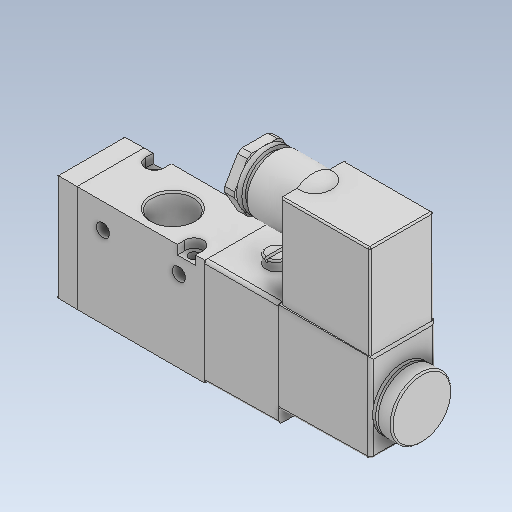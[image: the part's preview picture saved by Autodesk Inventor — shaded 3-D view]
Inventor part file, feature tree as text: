
AUTODESK INVENTOR PART (.ipt)
format: ipt  version: 2020 (Build 240168000, 168)  size: 314,368 bytes
history: native  units: in
note: dims shown in document units (in); Inventor stores cm internally (conversion verified against a paired STEP export)
features: fillet x3, chamfer x1
ambient origin geometry x8: Origin, YZ Plane, XZ Plane, XY Plane, X Axis, Y Axis, Z Axis, Center Point
bodies: Solid1 (feature_tree), Solid2 (feature_tree), Solid3 (feature_tree), Solid4 (feature_tree)
feature tree (4):
  chamfer  "Chamfer2"  [1 undecoded]
  fillet  "Fillet7"  [1 undecoded]
  fillet  "Fillet4"  [1 undecoded]
  fillet  "Fillet5"  [1 undecoded]
note: 4 required parameter values undecoded (feature->parameter linkage not recoverable at this tier; creation-order binding heuristic only, values carry confidence <= 0.55)
